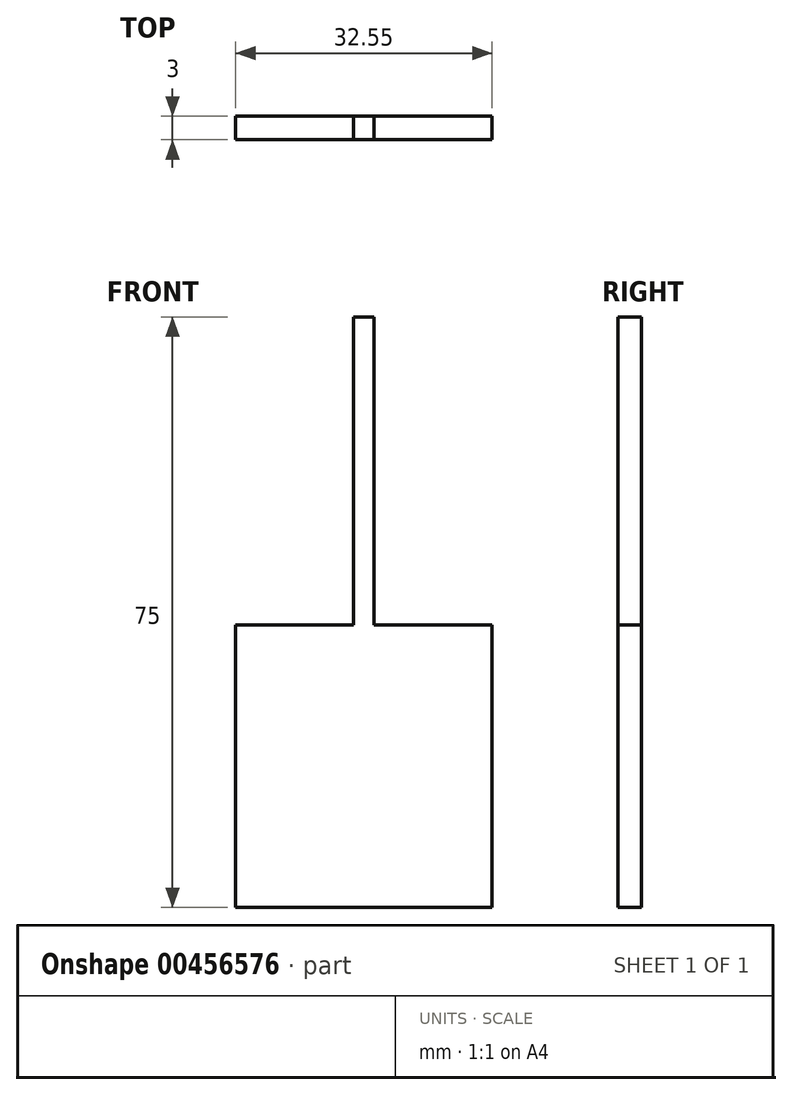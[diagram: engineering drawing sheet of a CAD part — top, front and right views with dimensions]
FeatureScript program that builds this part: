
annotation { "Feature Type Name" : "Feature", "Feature Type Description" : "" }
export const myFeature = defineFeature(function(context is Context, id is Id, definition is map)
    precondition{}
    {
        {
            var Q0;
            Q0=qCreatedBy(makeId("Front.planeOp"),FACE);
            var sketch = newSketch(context, id + "F0", { "sketchPlane" : qUnion([Q0])});
            skLineSegment(sketch, "E0.bottom", {"start": v(0, 17.92) * mm, "end": v(-15, 17.92) * mm});
            skLineSegment(sketch, "E0.top", {"start": v(0, -17.92) * mm, "end": v(-15, -17.92) * mm});
            skLineSegment(sketch, "E0.left", {"start": v(0, 17.92) * mm, "end": v(0, -17.92) * mm});
            skLineSegment(sketch, "E0.right", {"start": v(-15, 17.92) * mm, "end": v(-15, -17.92) * mm});
            skLineSegment(sketch, "E1.bottom", {"start": v(0, 57.08) * mm, "end": v(2.55, 57.08) * mm});
            skLineSegment(sketch, "E1.top", {"start": v(0, -17.92) * mm, "end": v(2.55, -17.92) * mm});
            skLineSegment(sketch, "E1.left", {"start": v(0, 57.08) * mm, "end": v(0, -17.92) * mm});
            skLineSegment(sketch, "E1.right", {"start": v(2.55, 57.08) * mm, "end": v(2.55, -17.92) * mm});
            skLineSegment(sketch, "E2.bottom", {"start": v(2.55, 17.92) * mm, "end": v(17.55, 17.92) * mm});
            skLineSegment(sketch, "E2.top", {"start": v(2.55, -17.92) * mm, "end": v(17.55, -17.92) * mm});
            skLineSegment(sketch, "E2.left", {"start": v(2.55, 17.92) * mm, "end": v(2.55, -17.92) * mm});
            skLineSegment(sketch, "E2.right", {"start": v(17.55, 17.92) * mm, "end": v(17.55, -17.92) * mm});
            skSolve(sketch);
        }
        {
            var Q0;
            Q0 = qSketchRegion(id + "F0", true);
            extrude(context, id + "F1", {"entities" : qUnion([Q0]), "depth" : 3 * mm, "offsetDistance" : 25 * mm});
        }
    });
